# Revit family: HERZ Water Filter For Hot Water 0554
name_source: partatom
category: Rohrzubehör
units: mm (PartAtom-declared; Revit-internal decimal feet)

## family parameters
Arbeitsebenenbasiert = Nein
Beim Laden mit Abzugskörper schneiden = Nein
Bemaßung runder Anschluss = Durchmesser verwenden
Gemeinsam genutzt = Nein
Immer vertikal = Ja
OmniClass-Nummer = 23.65.55.14
OmniClass-Titel = Valves for Liquid Services
Teiletyp = Unterbricht

## types (1)
- HERZ Water Filter For Hot Water 0554
    Application = The HERZ-Water filter is used in house entrance installations for potable water to protect the potable water against contamination.
In this way the proper functioning of the system is ensured.
Due to its compact design, the filter can be installed wherever space is restricted.
    Body = brass, CW617N
    Bowl = plastic Trogamid
    Cartridge = stainless steel, mesh size 100 μm
    D01 = 25.5 mm
    D02 = 22.75 mm  [stored 0.0746391 ft]
    H01 = 24 mm  [stored 0.0787402 ft]
    H02 = 45.5 mm  [stored 0.149278 ft]
    H03 = 67.5 mm
    H04 = 151 mm
    Hersteller = HERZ Armaturen Ges.m.b.H.
    Max. operating pressure = 1600000.0 Pa
    Max. operating temperature = 60 °C
    Medium = Water
    Model = Filter for hot water with body made of brass and bowl of Trogamid.
    Note = Pursuant to Article 33 of the REACH Regulation (EC No. 1907/2006), we are obliged to point out that the material lead is listed on the SVHC list and that all brass components manufactured in our products exceed 0.1% (w / w) lead (CAS: 7439-92-1 / EINECS: 231-100-4).
Since lead is a component part of an alloy, actual exposure is not possible and therefore no additional information on safe use is necessary.
    R01 = 12.5 mm  [stored 0.0410105 ft]
    R02 = 8 mm  [stored 0.0262467 ft]
    SCTWCODE = 02;00;02
    SCTWSEQ = FI;SBT_TYP_FI="FI";2
    SC_NennweiteBerechnet = 0
    T01 = 1 mm  [stored 0.00328084 ft]
    URL = www.herzvalves.com
    VRS01 = 10 mm  [stored 0.0328084 ft]
    W01 = 89.00°
    W02 = 88.00°

note: [stored X ft] marks values corroborated as IEEE doubles in the binary element streams (Revit-internal decimal feet)
